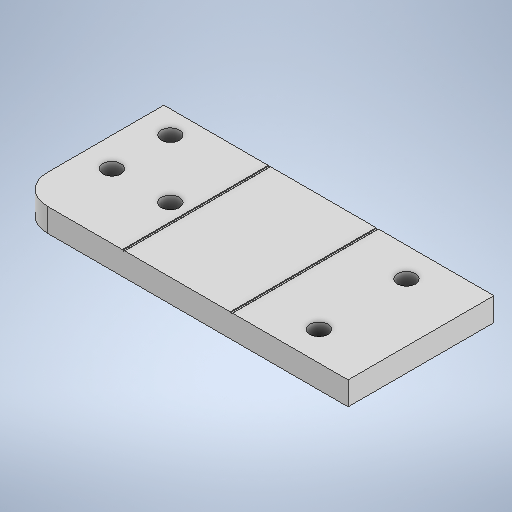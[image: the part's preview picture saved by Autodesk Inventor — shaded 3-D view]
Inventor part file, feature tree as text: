
AUTODESK INVENTOR PART (.ipt)
format: ipt  version: 2025 (Build 290162000, 162)  size: 259,072 bytes
history: native  units: mm
features: sketch x5, extrude x2, fillet x2
ambient origin geometry x8: Origin, YZ Plane, XZ Plane, XY Plane, X Axis, Y Axis, Z Axis, Center Point
bodies: Solid1 (feature_tree)
feature tree (9):
  extrude  "Extrusion1"  Depth=3.9mm
  extrude  "Extrusion2"  Depth=10.0mm
  fillet  "Fillet1"  Radius=25.0mm
  fillet  "Fillet2"  Radius=5.0mm
  sketch  "Sketch1"  dims[d0=3.1mm d1=3.9mm]
  sketch  "Sketch Rectangular Pattern1"  dims[d2=20.0mm d4=10.0mm d5=10.0mm d7=10.0mm d9=20.0mm d11=10.0mm d12=10.0mm d14=10.0mm d16=25.0mm d17=5.0mm]
  sketch  "Sketch Rectangular Pattern2"  dims[d18=56.58mm]
  sketch  "Sketch Rectangular Pattern3"  dims[d20=10.0mm d21=20.0mm d23=15.0mm d24=10.0mm d26=10.0mm d28=5.0mm d29=4.0mm d30=0.0mm d31=0.25mm d32=4.0mm d33=0.0mm d34=18.085mm d35=0.25mm d36=20.0mm d37=0.1mm d38=5.0mm]
  sketch  "Sketch2"  dims[d19=3.1mm]
